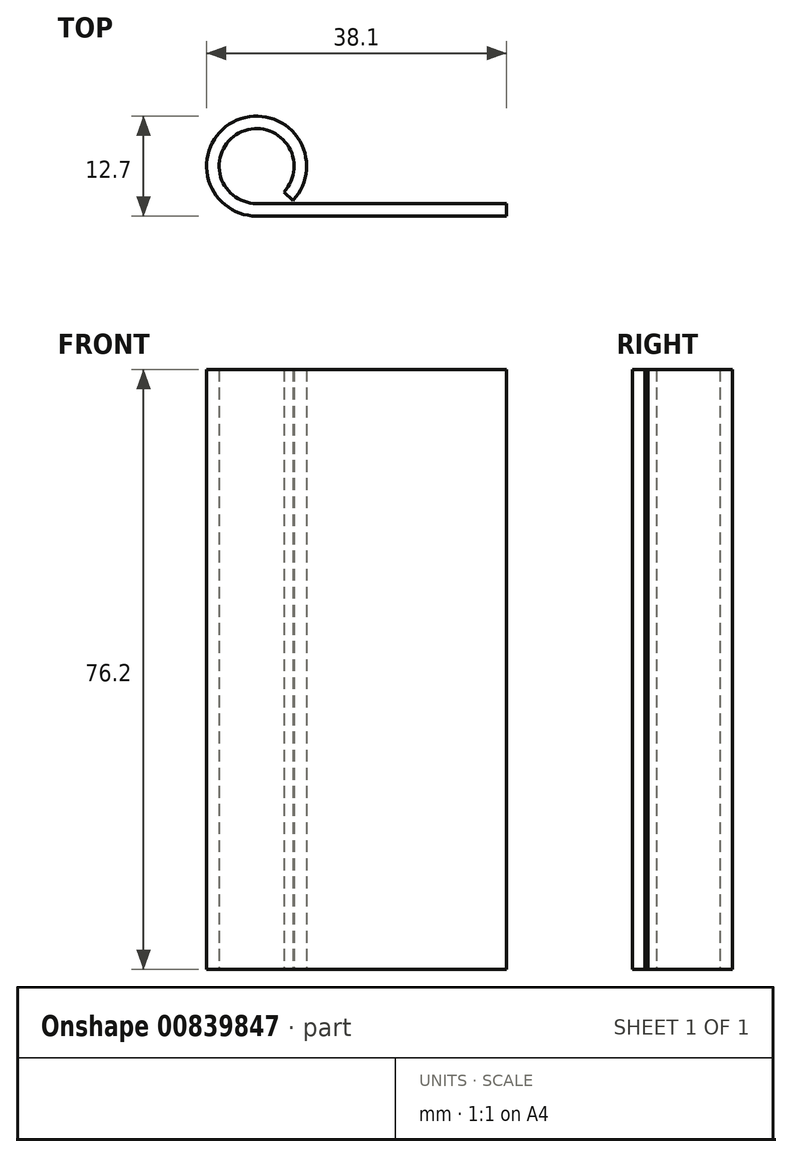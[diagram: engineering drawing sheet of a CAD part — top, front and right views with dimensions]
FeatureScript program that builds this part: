
annotation { "Feature Type Name" : "Feature", "Feature Type Description" : "" }
export const myFeature = defineFeature(function(context is Context, id is Id, definition is map)
    precondition{}
    {
        {
            var Q0;
            Q0=qCreatedBy(makeId("Top.planeOp"),FACE);
            var sketch = newSketch(context, id + "F0", { "sketchPlane" : qUnion([Q0])});
            skLineSegment(sketch, "E0", {"start": v(31.75, -4.76) * mm, "end": v(0, -4.76) * mm});
            skArc(sketch, "E1", {"start": v(4.61, -4.37) * mm, "mid": v(-2.51, 5.83) * mm, "end": v(0, -6.35) * mm});
            skArc(sketch, "E2.0", {"start": v(3.46, -3.27) * mm, "mid": v(-1.88, 4.37) * mm, "end": v(0, -4.76) * mm});
            skLineSegment(sketch, "E3", {"start": v(31.75, -6.35) * mm, "end": v(0, -6.35) * mm});
            skLineSegment(sketch, "E4", {"start": v(0, 0) * mm, "end": v(84.79, 0) * mm, "construction": true});
            skLineSegment(sketch, "E5", {"start": v(31.75, -4.76) * mm, "end": v(31.75, -6.35) * mm});
            skLineSegment(sketch, "E6", {"start": v(4.61, -4.37) * mm, "end": v(3.46, -3.27) * mm});
            skSolve(sketch);
        }
        {
            var Q0;
            Q0=makeQuery(id+"F0.imprint","IMPRINT",FACE,{"disambiguationData":[TD([[makeQuery(id+"F0.imprint","IMPRINT",EDGE,{"derivedFrom":sQuery(id+"F0.wireOp",EDGE,"E0")}),1.0]])]});
            extrude(context, id + "F1", {"entities" : qUnion([Q0]), "endBound" : BoundingType.SYMMETRIC, "depth" : 76.2 * mm});
        }
    });
